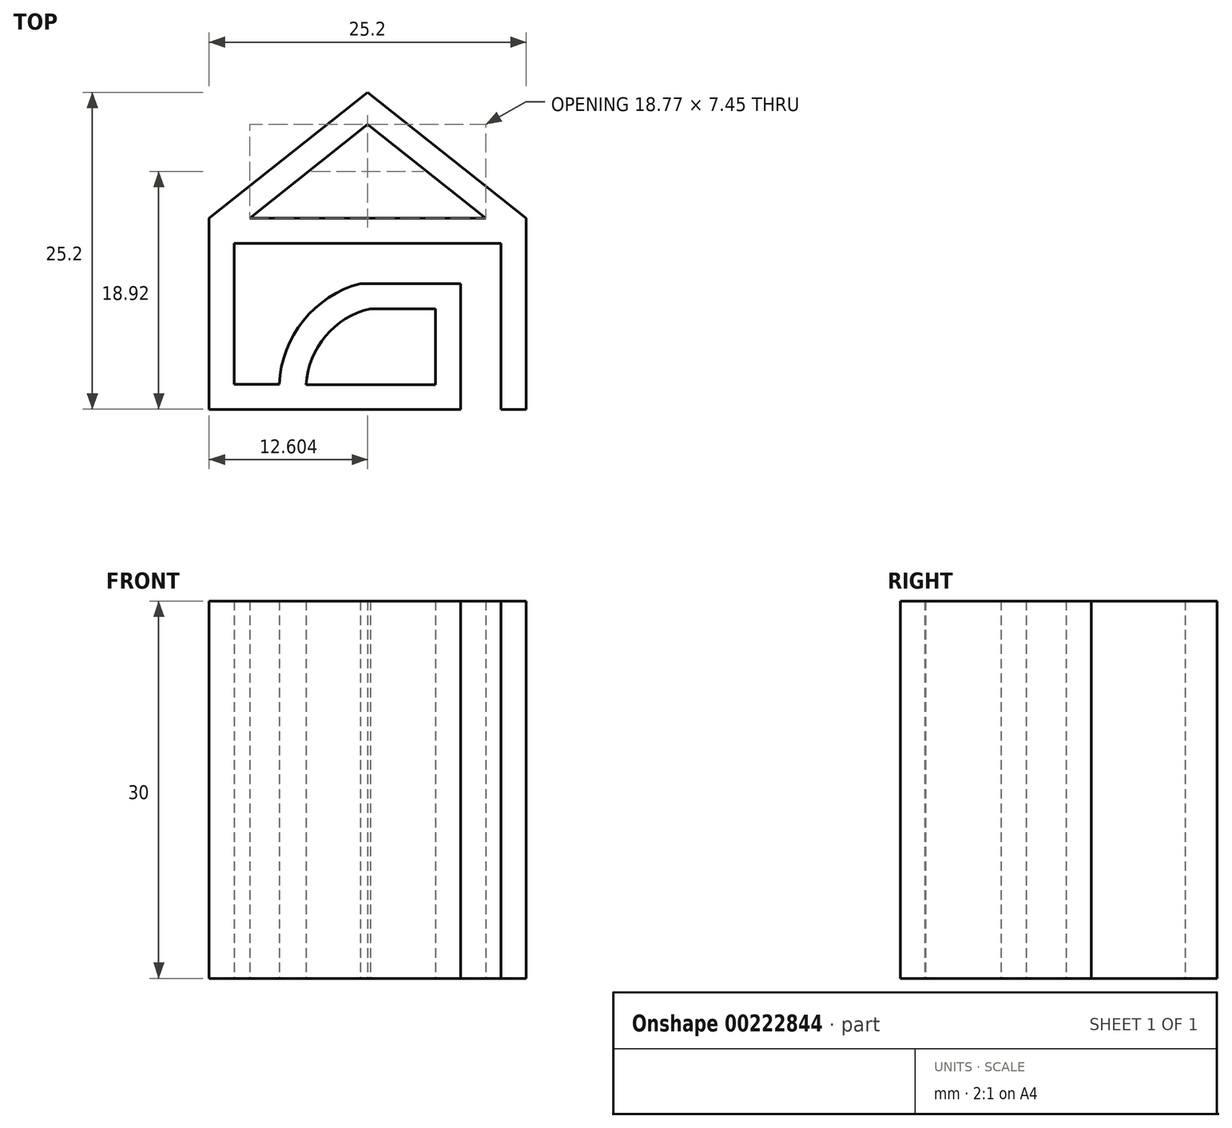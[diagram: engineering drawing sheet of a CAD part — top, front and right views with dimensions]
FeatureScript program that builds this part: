
annotation { "Feature Type Name" : "Feature", "Feature Type Description" : "" }
export const myFeature = defineFeature(function(context is Context, id is Id, definition is map)
    precondition{}
    {
        {
            var Q0;
            Q0=qCreatedBy(makeId("Top.planeOp"),FACE);
            var sketch = newSketch(context, id + "F0", { "sketchPlane" : qUnion([Q0])});
            skLineSegment(sketch, "E0", {"start": v(-8.6, 0.77) * mm, "end": v(11.4, 0.77) * mm, "construction": true});
            skLineSegment(sketch, "E1", {"start": v(11.4, 0.77) * mm, "end": v(11.4, -24.42) * mm, "construction": true});
            skLineSegment(sketch, "E2", {"start": v(11.4, -24.42) * mm, "end": v(9.4, -24.42) * mm, "construction": true});
            skLineSegment(sketch, "E3", {"start": v(9.4, -24.42) * mm, "end": v(9.4, -1.23) * mm, "construction": true});
            skLineSegment(sketch, "E4", {"start": v(9.4, -1.23) * mm, "end": v(-0.6, -1.23) * mm, "construction": true});
            skLineSegment(sketch, "E5", {"start": v(-8.6, 0.77) * mm, "end": v(-8.6, -9.23) * mm, "construction": true});
            skLineSegment(sketch, "E6", {"start": v(-8.6, -9.23) * mm, "end": v(-6.6, -9.23) * mm, "construction": true});
            skArc(sketch, "E7", {"start": v(-0.6, -1.23) * mm, "mid": v(-4.76, -4.36) * mm, "end": v(-6.6, -9.23) * mm, "construction": true});
            skArc(sketch, "E8.2", {"start": v(0.8, -1.83) * mm, "mid": v(-3.71, -4.79) * mm, "end": v(-5.63, -9.83) * mm});
            skLineSegment(sketch, "E8.3", {"start": v(-9.2, -9.83) * mm, "end": v(-5.63, -9.83) * mm});
            skLineSegment(sketch, "E8.4", {"start": v(-9.2, 1.37) * mm, "end": v(-9.2, -9.83) * mm});
            skLineSegment(sketch, "E9", {"start": v(12, 1.37) * mm, "end": v(12, -11.83) * mm});
            skLineSegment(sketch, "E10", {"start": v(12, -11.83) * mm, "end": v(14, -11.83) * mm});
            skLineSegment(sketch, "E11", {"start": v(14, -11.83) * mm, "end": v(14, 3.37) * mm});
            skLineSegment(sketch, "E12", {"start": v(-11.2, 3.37) * mm, "end": v(-11.2, -11.83) * mm});
            skLineSegment(sketch, "E13", {"start": v(8.8, -11.83) * mm, "end": v(8.8, -1.83) * mm});
            skLineSegment(sketch, "E14", {"start": v(8.8, -1.83) * mm, "end": v(0.8, -1.83) * mm});
            skArc(sketch, "E15.0", {"start": v(1.6, -3.83) * mm, "mid": v(-1.95, -6) * mm, "end": v(-3.5, -9.87) * mm});
            skLineSegment(sketch, "E16", {"start": v(1.6, -3.83) * mm, "end": v(6.8, -3.83) * mm});
            skLineSegment(sketch, "E17", {"start": v(-3.5, -9.87) * mm, "end": v(6.8, -9.87) * mm});
            skLineSegment(sketch, "E18", {"start": v(6.8, -9.87) * mm, "end": v(6.8, -3.83) * mm});
            skLineSegment(sketch, "E19", {"start": v(-9.2, 1.37) * mm, "end": v(12, 1.37) * mm});
            skLineSegment(sketch, "E20", {"start": v(8.8, -11.83) * mm, "end": v(-11.2, -11.83) * mm});
            skLineSegment(sketch, "E21", {"start": v(-11.2, 3.37) * mm, "end": v(1.4, 13.37) * mm});
            skLineSegment(sketch, "E22", {"start": v(1.4, 13.37) * mm, "end": v(14, 3.37) * mm});
            skLineSegment(sketch, "E23", {"start": v(1.4, 1.37) * mm, "end": v(1.4, 12.2) * mm, "construction": true});
            skLineSegment(sketch, "E24.0", {"start": v(1.4, 10.81) * mm, "end": v(10.79, 3.37) * mm});
            skLineSegment(sketch, "E24.1", {"start": v(-7.98, 3.37) * mm, "end": v(1.4, 10.81) * mm});
            skLineSegment(sketch, "E25.0", {"start": v(-7.98, 3.37) * mm, "end": v(10.79, 3.37) * mm});
            skPoint(sketch, "E26", {"position": v(-7.98, 3.37) * mm});
            skPoint(sketch, "E27", {"position": v(10.79, 3.37) * mm});
            skPoint(sketch, "E28", {"position": v(12.76, 1.8) * mm});
            skSolve(sketch);
        }
        {
            var Q0;
            Q0=makeQuery(id+"F0.imprint","IMPRINT",FACE,{"disambiguationData":[TD([[makeQuery(id+"F0.imprint","IMPRINT",EDGE,{"derivedFrom":sQuery(id+"F0.wireOp",EDGE,"E8.2")}),1.0]])]});
            extrude(context, id + "F1", {"entities" : qUnion([Q0]), "depth" : 30 * mm});
        }
    });
